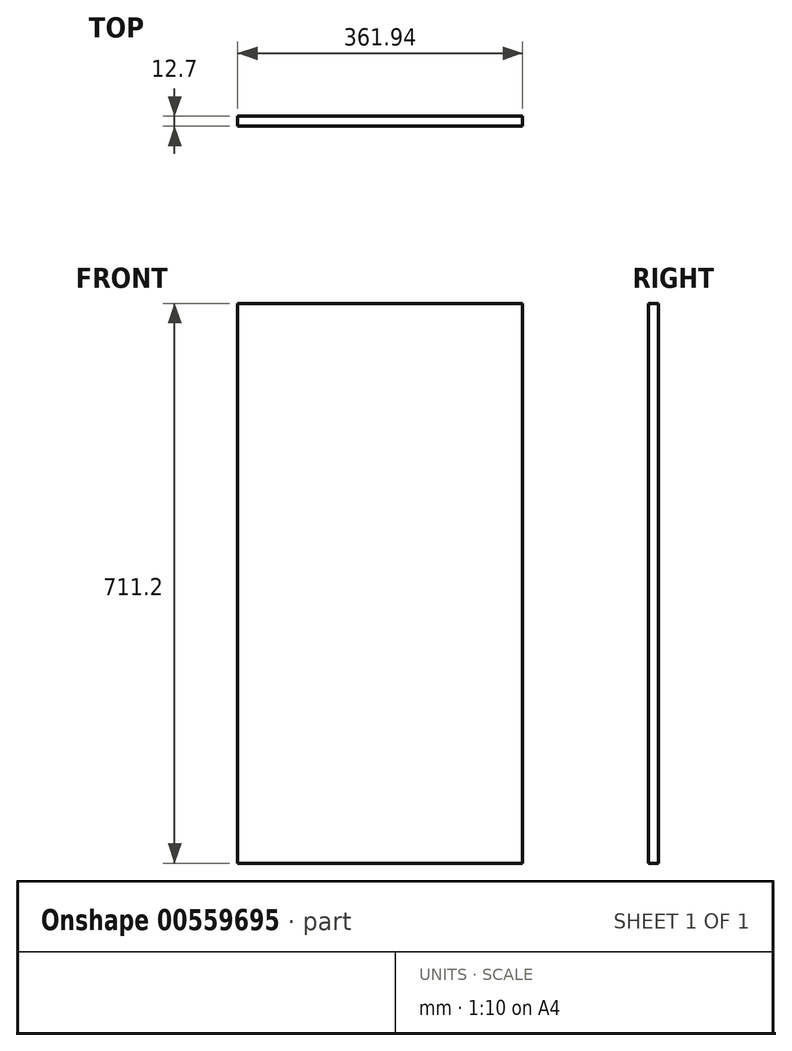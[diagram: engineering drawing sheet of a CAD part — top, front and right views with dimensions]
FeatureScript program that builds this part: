
annotation { "Feature Type Name" : "Feature", "Feature Type Description" : "" }
export const myFeature = defineFeature(function(context is Context, id is Id, definition is map)
    precondition{}
    {
        {
            var Q0;
            Q0=qCreatedBy(makeId("Front.planeOp"),FACE);
            var sketch = newSketch(context, id + "F0", { "sketchPlane" : qUnion([Q0])});
            skLineSegment(sketch, "E0.bottom", {"start": v(180.97, -355.6) * mm, "end": v(-180.98, -355.6) * mm});
            skLineSegment(sketch, "E0.top", {"start": v(180.98, 355.6) * mm, "end": v(-180.97, 355.6) * mm});
            skLineSegment(sketch, "E0.left", {"start": v(180.97, -355.6) * mm, "end": v(180.98, 355.6) * mm});
            skLineSegment(sketch, "E0.right", {"start": v(-180.98, -355.6) * mm, "end": v(-180.97, 355.6) * mm});
            skPoint(sketch, "E0.middle", {"position": v(0, 0) * mm});
            skSolve(sketch);
        }
        {
            var Q0;
            Q0 = qSketchRegion(id + "F0", true);
            extrude(context, id + "F1", {"entities" : qUnion([Q0]), "depth" : 12.7 * mm, "offsetDistance" : 25.4 * mm});
        }
    });
